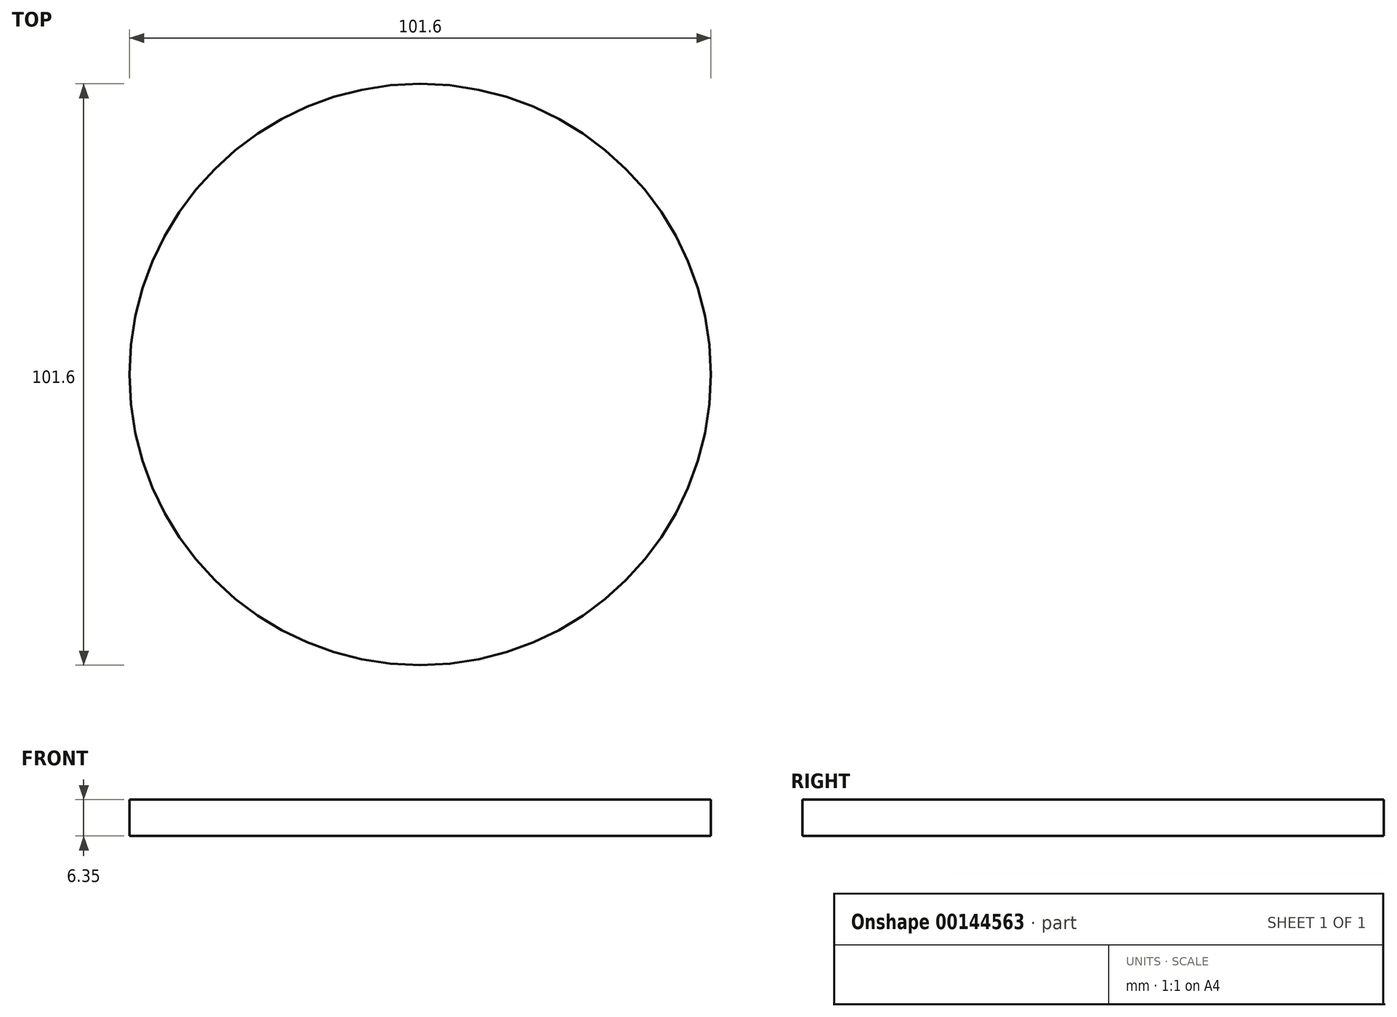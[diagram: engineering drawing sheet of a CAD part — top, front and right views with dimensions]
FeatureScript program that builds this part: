
annotation { "Feature Type Name" : "Feature", "Feature Type Description" : "" }
export const myFeature = defineFeature(function(context is Context, id is Id, definition is map)
    precondition{}
    {
        {
            var Q0;
            Q0=qCreatedBy(makeId("Top.planeOp"),FACE);
            var sketch = newSketch(context, id + "F0", { "sketchPlane" : qUnion([Q0])});
            skCircle(sketch, "E0", {"center": v(0, 0) * mm, "radius": 50.8 * mm});
            skSolve(sketch);
        }
        {
            var Q0;
            Q0 = qSketchRegion(id + "F0", true);
            extrude(context, id + "F1", {"entities" : qUnion([Q0]), "depth" : 6.35 * mm});
        }
    });
